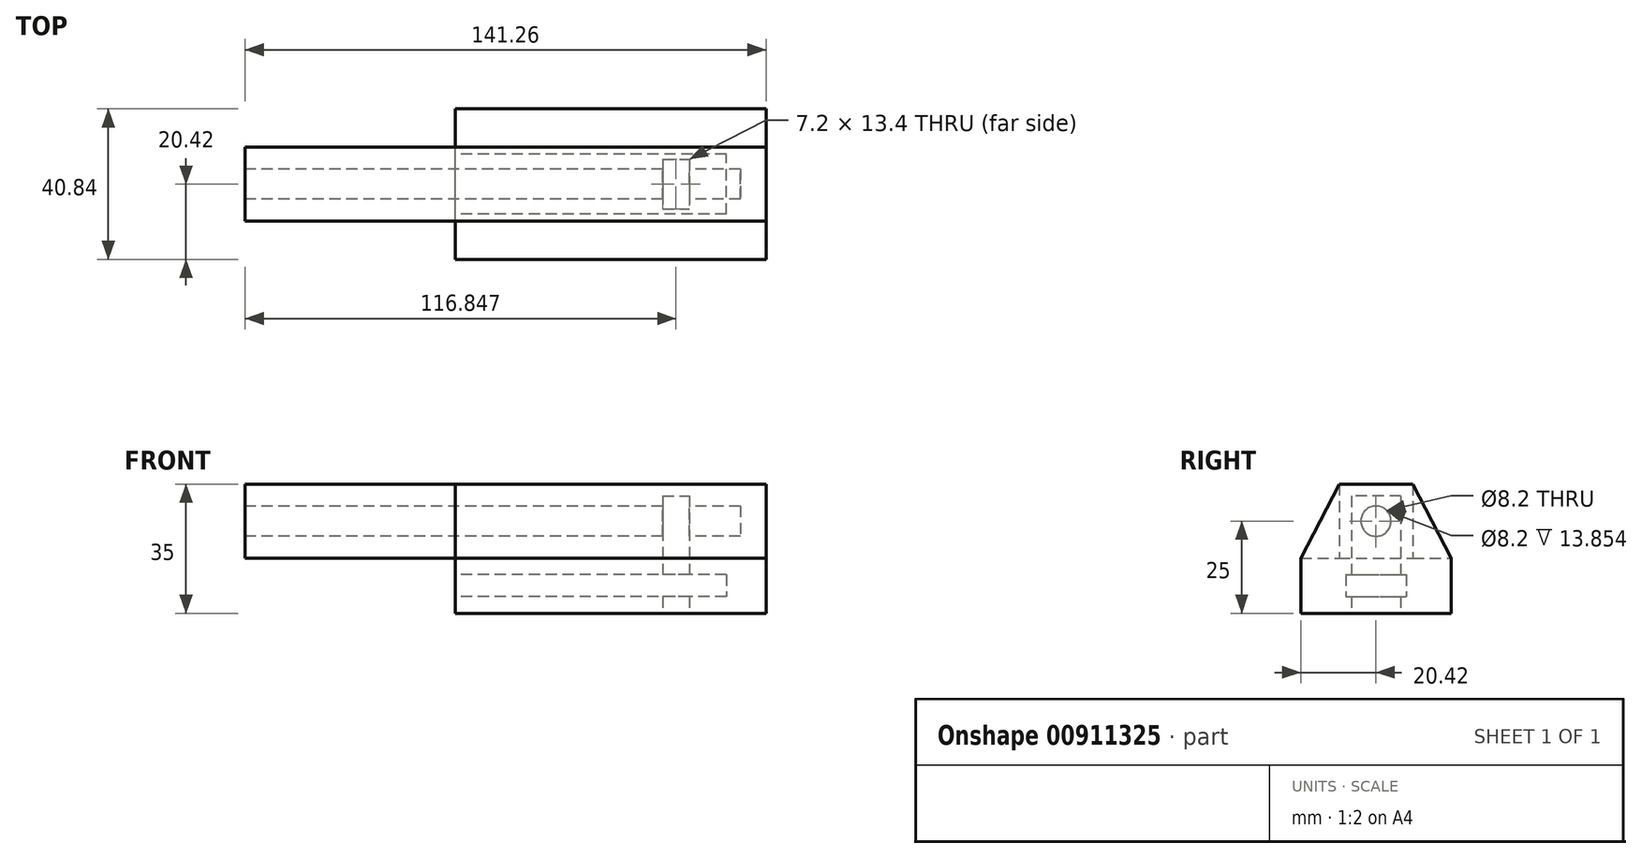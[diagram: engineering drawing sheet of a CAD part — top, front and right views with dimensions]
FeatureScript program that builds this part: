
annotation { "Feature Type Name" : "Feature", "Feature Type Description" : "" }
export const myFeature = defineFeature(function(context is Context, id is Id, definition is map)
    precondition{}
    {
        {
            var Q0;
            Q0=qCreatedBy(makeId("Top.planeOp"),FACE);
            var sketch = newSketch(context, id + "F0", { "sketchPlane" : qUnion([Q0])});
            skLineSegment(sketch, "E0.bottom", {"start": v(37.5, -8) * mm, "end": v(-37.5, -8) * mm});
            skLineSegment(sketch, "E0.top", {"start": v(37.5, 8) * mm, "end": v(-37.5, 8) * mm});
            skLineSegment(sketch, "E0.left", {"start": v(37.5, -8) * mm, "end": v(37.5, 8) * mm});
            skLineSegment(sketch, "E0.right", {"start": v(-37.5, -8) * mm, "end": v(-37.5, 8) * mm});
            skPoint(sketch, "E0.middle", {"position": v(0, 0) * mm});
            skLineSegment(sketch, "E1.bottom", {"start": v(42.12, -20.42) * mm, "end": v(-42.12, -20.42) * mm});
            skLineSegment(sketch, "E1.top", {"start": v(42.12, 20.42) * mm, "end": v(-42.12, 20.42) * mm});
            skLineSegment(sketch, "E1.left", {"start": v(42.12, -20.42) * mm, "end": v(42.12, 20.42) * mm});
            skLineSegment(sketch, "E1.right", {"start": v(-42.12, -20.42) * mm, "end": v(-42.12, 20.42) * mm});
            skSolve(sketch);
        }
        {
            var Q0;
            Q0=makeQuery(id+"F0.imprint","IMPRINT",FACE,{"disambiguationData":[TD([[makeQuery(id+"F0.imprint","IMPRINT",EDGE,{"derivedFrom":sQuery(id+"F0.wireOp",EDGE,"E0.bottom")}),1.0]])]});
            var Q1;
            Q1=makeQuery(id+"F0.imprint","IMPRINT",FACE,{"disambiguationData":[TD([[makeQuery(id+"F0.imprint","IMPRINT",EDGE,{"derivedFrom":sQuery(id+"F0.wireOp",EDGE,"E0.bottom")}),-1.0]])]});
            extrude(context, id + "F1", {"entities" : qUnion([Q0, Q1]), "endBound" : BoundingType.SYMMETRIC, "depth" : 15 * mm, "offsetDistance" : 25 * mm});
        }
        {
            var Q0;
            Q0=makeQuery(id+"F1.opExtrude","SWEPT_FACE",FACE,{"disambiguationData":[OSD([sQuery(id+"F0.wireOp",EDGE,"E1.right")])]});
            var sketch = newSketch(context, id + "F2", { "sketchPlane" : qUnion([Q0])});
            skLineSegment(sketch, "E2.bottom", {"start": v(8.15, 3) * mm, "end": v(-8.15, 3) * mm});
            skLineSegment(sketch, "E2.top", {"start": v(8.15, -3) * mm, "end": v(-8.15, -3) * mm});
            skLineSegment(sketch, "E2.left", {"start": v(8.15, 3) * mm, "end": v(8.15, -3) * mm});
            skLineSegment(sketch, "E2.right", {"start": v(-8.15, 3) * mm, "end": v(-8.15, -3) * mm});
            skPoint(sketch, "E2.middle", {"position": v(0, 0) * mm});
            skSolve(sketch);
        }
        {
            var Q0;
            Q0=makeQuery(id+"F2.imprint","IMPRINT",FACE,{"disambiguationData":[TD([[makeQuery(id+"F2.imprint","IMPRINT",EDGE,{"derivedFrom":sQuery(id+"F2.wireOp",EDGE,"E2.bottom")}),1.0]])]});
            extrude(context, id + "F3", {"entities" : qUnion([Q0]), "operationType" : NewBodyOperationType.REMOVE, "oppositeDirection" : true, "depth" : 73.5 * mm, "offsetDistance" : 25 * mm});
        }
        {
            var Q0;
            Q0=makeQuery(id+"F1.opExtrude","CAP_FACE",FACE,{"disambiguationData":[OSD([sQuery(id+"F0.wireOp",EDGE,"E1.bottom"),sQuery(id+"F0.wireOp",EDGE,"E1.top"),sQuery(id+"F0.wireOp",EDGE,"E1.left"),sQuery(id+"F0.wireOp",EDGE,"E1.right")])],"isStart":false});
            var sketch = newSketch(context, id + "F4", { "sketchPlane" : qUnion([Q0])});
            skLineSegment(sketch, "E3.bottom", {"start": v(42.12, -10) * mm, "end": v(-99.14, -10) * mm});
            skLineSegment(sketch, "E3.top", {"start": v(42.12, 10) * mm, "end": v(-99.14, 10) * mm});
            skLineSegment(sketch, "E3.left", {"start": v(42.12, -10) * mm, "end": v(42.12, 10) * mm});
            skLineSegment(sketch, "E3.right", {"start": v(-99.14, -10) * mm, "end": v(-99.14, 10) * mm});
            skPoint(sketch, "E3.middle", {"position": v(-28.5, 0) * mm});
            skPoint(sketch, "E3.middle.positionSnap0", {"position": v(-42.12, 0) * mm});
            skPoint(sketch, "E3.centerSnap0", {"position": v(-42.12, 0) * mm});
            skSolve(sketch);
        }
        {
            var Q0;
            {var subQ0=sQuery(id+"F4.wireOp",EDGE,"E3.right");Q0=makeQuery(id+"F4.imprint","IMPRINT",FACE,{"disambiguationData":[TD([[makeQuery(id+"F4.imprint","IMPRINT",EDGE,{"derivedFrom":subQ0}),-1.0]])]});}
            var Q1;
            {var subQ0=sQuery(id+"F4.wireOp",EDGE,"E3.left");Q1=makeQuery(id+"F4.imprint","IMPRINT",FACE,{"disambiguationData":[TD([[makeQuery(id+"F4.imprint","IMPRINT",EDGE,{"derivedFrom":subQ0}),1.0]])]});}
            extrude(context, id + "F5", {"entities" : qUnion([Q0, Q1]), "operationType" : NewBodyOperationType.ADD, "depth" : 20 * mm, "offsetDistance" : 25 * mm});
        }
        {
            var Q0;
            Q0=makeQuery(id+"F5.opExtrude","SWEPT_FACE",FACE,{"disambiguationData":[OSD([sQuery(id+"F4.wireOp",EDGE,"E3.right")])]});
            var sketch = newSketch(context, id + "F6", { "sketchPlane" : qUnion([Q0])});
            skCircle(sketch, "E4", {"center": v(0, 17.5) * mm, "radius": 4.1 * mm});
            skPoint(sketch, "E4.centerSnap0", {"position": v(-10, 17.5) * mm});
            skPoint(sketch, "E4.centerSnap1", {"position": v(0, 27.5) * mm});
            skSolve(sketch);
        }
        {
            var Q0;
            Q0=makeQuery(id+"F6.imprint","IMPRINT",FACE,{"disambiguationData":[TD([[makeQuery(id+"F6.imprint","IMPRINT",EDGE,{"derivedFrom":sQuery(id+"F6.wireOp",EDGE,"E4")}),1.0]])]});
            extrude(context, id + "F7", {"entities" : qUnion([Q0]), "operationType" : NewBodyOperationType.REMOVE, "oppositeDirection" : true, "depth" : 134.3 * mm, "offsetDistance" : 25 * mm});
        }
        {
            var Q0;
            Q0=makeQuery(id+"F5.boolean.opBoolean","MERGE",FACE,{"derivedFrom":[makeQuery(id+"F1.opExtrude","SWEPT_FACE",FACE,{"disambiguationData":[OSD([sQuery(id+"F0.wireOp",EDGE,"E1.left")])]}),makeQuery(id+"F5.opExtrude","SWEPT_FACE",FACE,{"disambiguationData":[OSD([sQuery(id+"F4.wireOp",EDGE,"E3.left")])]})]});
            var sketch = newSketch(context, id + "F8", { "sketchPlane" : qUnion([Q0])});
            skLineSegment(sketch, "E5", {"start": v(-10, 27.5) * mm, "end": v(-20.42, 7.5) * mm});
            skLineSegment(sketch, "E6", {"start": v(-20.42, 7.5) * mm, "end": v(-10, 7.5) * mm});
            skLineSegment(sketch, "E7", {"start": v(-10, 7.5) * mm, "end": v(-10, 27.5) * mm});
            skLineSegment(sketch, "E8.MirrorCS", {"start": v(10, 27.5) * mm, "end": v(20.42, 7.5) * mm});
            skLineSegment(sketch, "E9.MirrorCS", {"start": v(10, 7.5) * mm, "end": v(10, 27.5) * mm});
            skLineSegment(sketch, "E10.MirrorCS", {"start": v(20.42, 7.5) * mm, "end": v(10, 7.5) * mm});
            skSolve(sketch);
        }
        {
            var Q0;
            Q0=makeQuery(id+"F8.imprint","IMPRINT",FACE,{"disambiguationData":[TD([[makeQuery(id+"F8.imprint","IMPRINT",EDGE,{"derivedFrom":sQuery(id+"F8.wireOp",EDGE,"E5")}),1.0]])]});
            var Q1;
            Q1=makeQuery(id+"F8.imprint","IMPRINT",FACE,{"disambiguationData":[TD([[makeQuery(id+"F8.imprint","IMPRINT",EDGE,{"derivedFrom":sQuery(id+"F8.wireOp",EDGE,"E8.MirrorCS")}),-1.0]])]});
            extrude(context, id + "F9", {"entities" : qUnion([Q0, Q1]), "operationType" : NewBodyOperationType.ADD, "oppositeDirection" : true, "depth" : 84.23 * mm, "offsetDistance" : 25 * mm});
        }
        {
            var Q0;
            Q0=makeQuery(id+"F1.opExtrude","CAP_FACE",FACE,{"disambiguationData":[OSD([sQuery(id+"F0.wireOp",EDGE,"E1.bottom"),sQuery(id+"F0.wireOp",EDGE,"E1.top"),sQuery(id+"F0.wireOp",EDGE,"E1.left"),sQuery(id+"F0.wireOp",EDGE,"E1.right")])],"isStart":true});
            var sketch = newSketch(context, id + "F10", { "sketchPlane" : qUnion([Q0])});
            skLineSegment(sketch, "E11.bottom", {"start": v(14.1, -6.7) * mm, "end": v(21.3, -6.7) * mm});
            skLineSegment(sketch, "E11.top", {"start": v(14.1, 6.7) * mm, "end": v(21.3, 6.7) * mm});
            skLineSegment(sketch, "E11.left", {"start": v(14.1, -6.7) * mm, "end": v(14.1, 6.7) * mm});
            skLineSegment(sketch, "E11.right", {"start": v(21.3, -6.7) * mm, "end": v(21.3, 6.7) * mm});
            skPoint(sketch, "E11.middle", {"position": v(17.7, 0) * mm});
            skSolve(sketch);
        }
        {
            var Q0;
            Q0=makeQuery(id+"F10.imprint","IMPRINT",FACE,{"disambiguationData":[TD([[makeQuery(id+"F10.imprint","IMPRINT",EDGE,{"derivedFrom":sQuery(id+"F10.wireOp",EDGE,"E11.bottom")}),1.0]])]});
            extrude(context, id + "F11", {"entities" : qUnion([Q0]), "operationType" : NewBodyOperationType.REMOVE, "oppositeDirection" : true, "depth" : 31.8 * mm, "offsetDistance" : 25 * mm});
        }
    });
